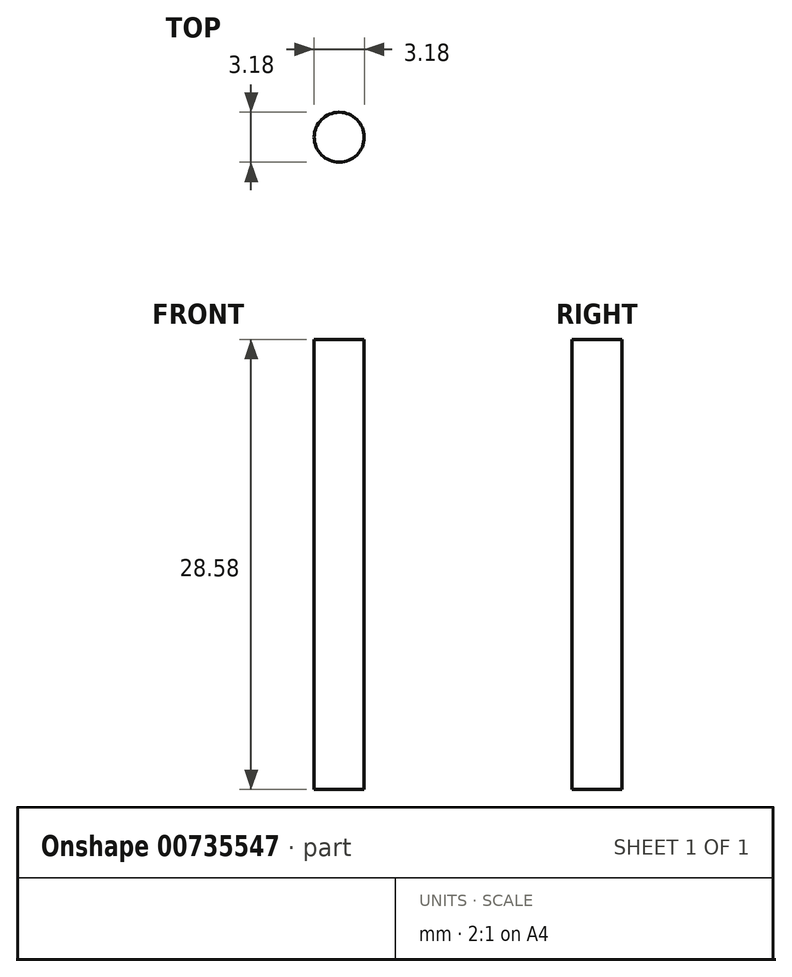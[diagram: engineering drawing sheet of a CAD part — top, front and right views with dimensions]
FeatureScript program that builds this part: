
annotation { "Feature Type Name" : "Feature", "Feature Type Description" : "" }
export const myFeature = defineFeature(function(context is Context, id is Id, definition is map)
    precondition{}
    {
        {
            var Q0;
            Q0=qCreatedBy(makeId("Top.planeOp"),FACE);
            var sketch = newSketch(context, id + "F0", { "sketchPlane" : qUnion([Q0])});
            skCircle(sketch, "E0", {"center": v(0, 0) * mm, "radius": 1.59 * mm});
            skSolve(sketch);
        }
        {
            var Q0;
            Q0=makeQuery(id+"F0.imprint","IMPRINT",FACE,{"disambiguationData":[TD([[makeQuery(id+"F0.imprint","IMPRINT",EDGE,{"derivedFrom":sQuery(id+"F0.wireOp",EDGE,"E0")}),1.0]])]});
            extrude(context, id + "F1", {"entities" : qUnion([Q0]), "depth" : 28.57 * mm, "offsetDistance" : 25.4 * mm});
        }
    });
